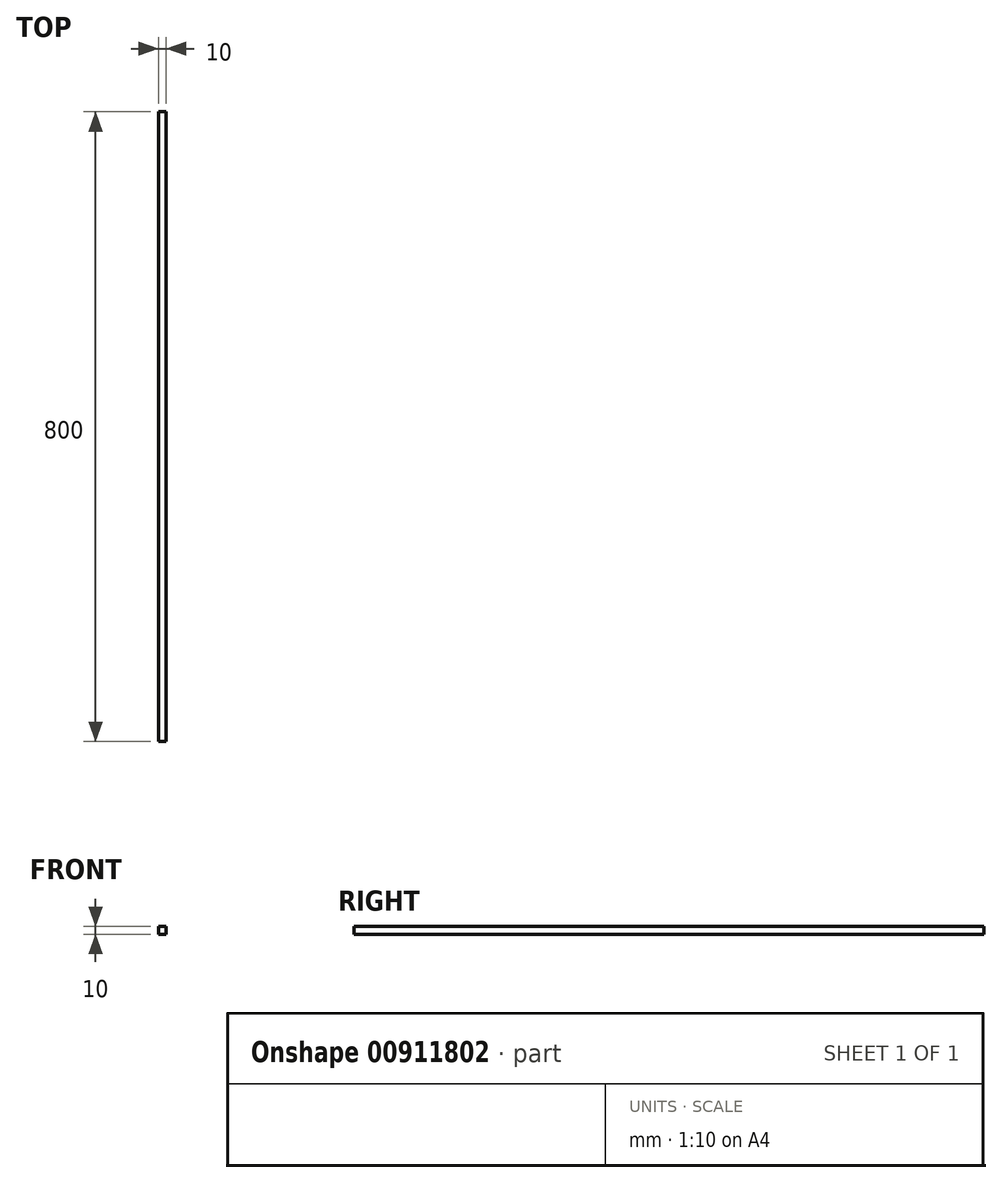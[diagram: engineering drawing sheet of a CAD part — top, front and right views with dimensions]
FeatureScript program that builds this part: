
annotation { "Feature Type Name" : "Feature", "Feature Type Description" : "" }
export const myFeature = defineFeature(function(context is Context, id is Id, definition is map)
    precondition{}
    {
        {
            var Q0;
            Q0=qCreatedBy(makeId("Front.planeOp"),FACE);
            var sketch = newSketch(context, id + "F0", { "sketchPlane" : qUnion([Q0])});
            skLineSegment(sketch, "E0.bottom", {"start": v(-5, 5) * mm, "end": v(5, 5) * mm});
            skLineSegment(sketch, "E0.top", {"start": v(-5, -5) * mm, "end": v(5, -5) * mm});
            skLineSegment(sketch, "E0.left", {"start": v(-5, 5) * mm, "end": v(-5, -5) * mm});
            skLineSegment(sketch, "E0.right", {"start": v(5, 5) * mm, "end": v(5, -5) * mm});
            skPoint(sketch, "E0.middle", {"position": v(0, 0) * mm});
            skSolve(sketch);
        }
        {
            var Q0;
            Q0=qSketchRegion(id+"F0",true);
            extrude(context, id + "F1", {"entities" : qUnion([Q0]), "depth" : 800 * mm, "offsetDistance" : 25 * mm});
        }
    });
